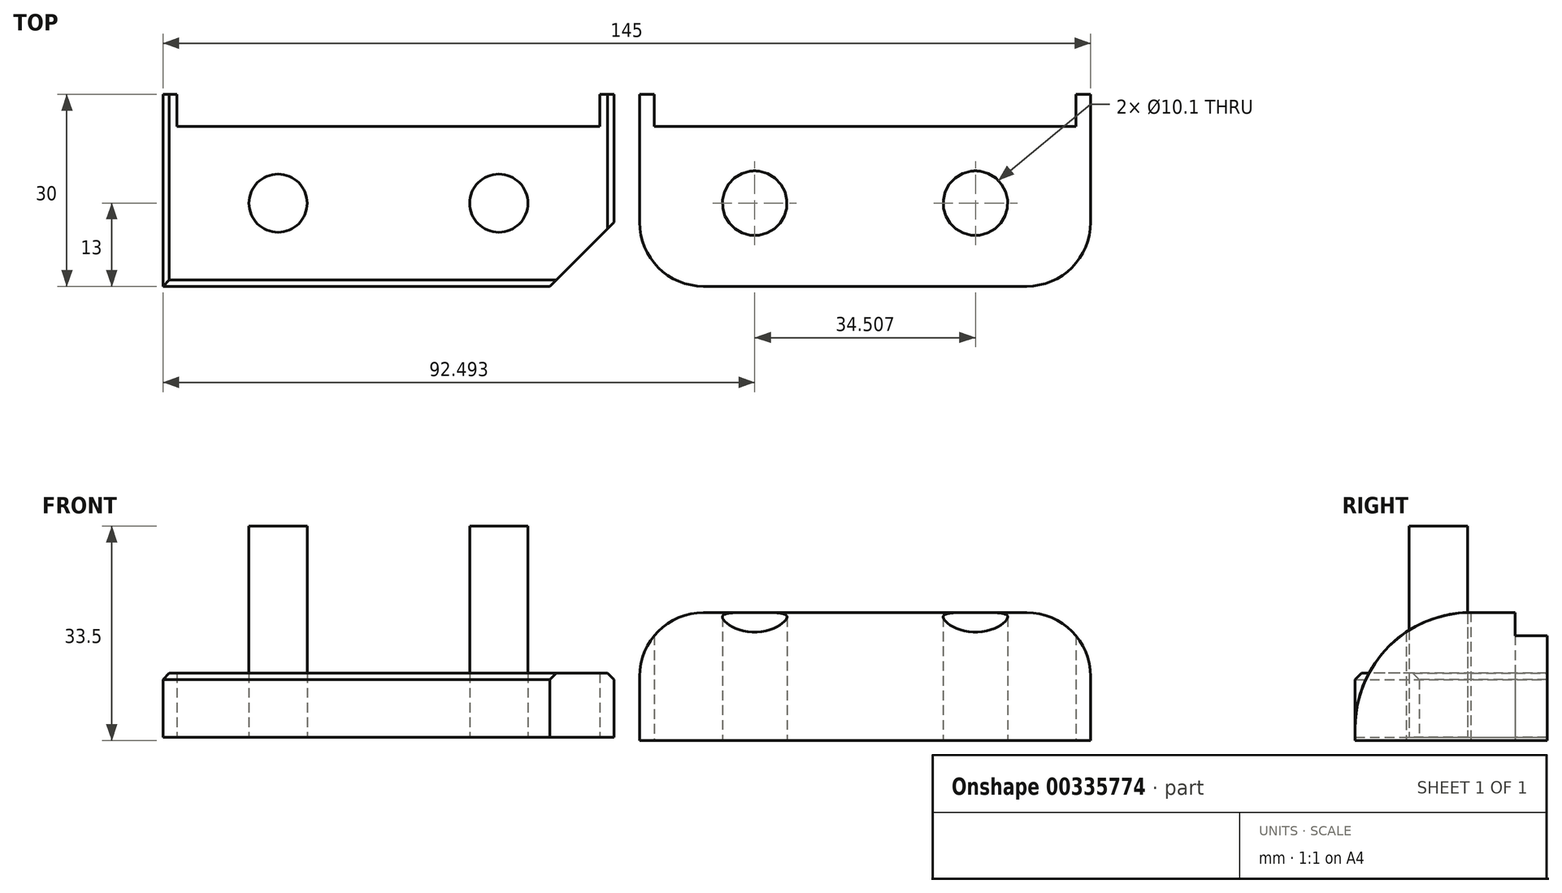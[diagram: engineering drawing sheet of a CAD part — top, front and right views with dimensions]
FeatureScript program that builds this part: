
annotation { "Feature Type Name" : "Feature", "Feature Type Description" : "" }
export const myFeature = defineFeature(function(context is Context, id is Id, definition is map)
    precondition{}
    {
        {
            var Q0;
            Q0=qCreatedBy(makeId("Front.planeOp"),FACE);
            var sketch = newSketch(context, id + "F0", { "sketchPlane" : qUnion([Q0])});
            skLineSegment(sketch, "E0.bottom", {"start": v(-53.86, 25) * mm, "end": v(16.64, 25) * mm});
            skLineSegment(sketch, "E0.top", {"start": v(-53.86, 5) * mm, "end": v(16.64, 5) * mm});
            skLineSegment(sketch, "E0.left", {"start": v(-53.86, 25) * mm, "end": v(-53.86, 5) * mm});
            skLineSegment(sketch, "E0.right", {"start": v(16.64, 25) * mm, "end": v(16.64, 5) * mm});
            skLineSegment(sketch, "E1.bottom", {"start": v(-53.86, 0) * mm, "end": v(16.64, 0) * mm});
            skLineSegment(sketch, "E1.top", {"start": v(-53.86, -10) * mm, "end": v(16.64, -10) * mm});
            skLineSegment(sketch, "E1.left", {"start": v(-53.86, 0) * mm, "end": v(-53.86, -10) * mm});
            skLineSegment(sketch, "E1.right", {"start": v(16.64, 0) * mm, "end": v(16.64, -10) * mm});
            skSolve(sketch);
        }
        {
            var Q0;
            Q0=makeQuery(id+"F0.imprint","IMPRINT",FACE,{"disambiguationData":[TD([[makeQuery(id+"F0.imprint","IMPRINT",EDGE,{"derivedFrom":sQuery(id+"F0.wireOp",EDGE,"E0.bottom")}),-1.0]])]});
            var Q1;
            Q1=makeQuery(id+"F0.imprint","IMPRINT",FACE,{"disambiguationData":[TD([[makeQuery(id+"F0.imprint","IMPRINT",EDGE,{"derivedFrom":sQuery(id+"F0.wireOp",EDGE,"E1.bottom")}),-1.0]])]});
            extrude(context, id + "F1", {"entities" : qUnion([Q0, Q1]), "depth" : 25 * mm});
        }
        {
            var Q0;
            Q0=qCreatedBy(makeId("Top.planeOp"),FACE);
            var sketch = newSketch(context, id + "F2", { "sketchPlane" : qUnion([Q0])});
            skPoint(sketch, "E2", {"position": v(-35.87, -12) * mm});
            skPoint(sketch, "E3", {"position": v(-1.36, -12) * mm});
            skSolve(sketch);
        }
        {
            var Q0;
            Q0=qCreatedBy(makeId("Top.planeOp"),FACE);
            var sketch = newSketch(context, id + "F3", { "sketchPlane" : qUnion([Q0])});
            skCircle(sketch, "E4", {"center": v(-35.87, -12) * mm, "radius": 4.55 * mm});
            skCircle(sketch, "E5", {"center": v(-1.36, -12) * mm, "radius": 4.55 * mm});
            skSolve(sketch);
        }
        {
            var Q0;
            Q0=makeQuery(id+"F3.imprint","IMPRINT",FACE,{"disambiguationData":[TD([[makeQuery(id+"F3.imprint","IMPRINT",EDGE,{"derivedFrom":sQuery(id+"F3.wireOp",EDGE,"E4")}),1.0]])]});
            var Q1;
            Q1=makeQuery(id+"F3.imprint","IMPRINT",FACE,{"disambiguationData":[TD([[makeQuery(id+"F3.imprint","IMPRINT",EDGE,{"derivedFrom":sQuery(id+"F3.wireOp",EDGE,"E5")}),1.0]])]});
            var Q2;
            Q2=sQuery(id+"F3.wireOp",EDGE,"E4");
            var Q3;
            Q3=sQuery(id+"F3.wireOp",EDGE,"E5");
            extrude(context, id + "F4", {"entities" : qUnion([Q0, Q1]), "surfaceEntities" : qUnion([Q2, Q3]), "depth" : 33 * mm});
        }
        {
            var Q0;
            Q0=makeQuery(id+"F1.opExtrude","CAP_FACE",FACE,{"disambiguationData":[OSD([sQuery(id+"F0.wireOp",EDGE,"E0.bottom"),sQuery(id+"F0.wireOp",EDGE,"E0.top"),sQuery(id+"F0.wireOp",EDGE,"E0.left"),sQuery(id+"F0.wireOp",EDGE,"E0.right")])],"isStart":true});
            var sketch = newSketch(context, id + "F5", { "sketchPlane" : qUnion([Q0])});
            skLineSegment(sketch, "E6.bottom", {"start": v(51.56, 25) * mm, "end": v(53.86, 25) * mm});
            skLineSegment(sketch, "E6.top", {"start": v(51.56, 5) * mm, "end": v(53.86, 5) * mm});
            skLineSegment(sketch, "E6.left", {"start": v(51.56, 25) * mm, "end": v(51.56, 5) * mm});
            skLineSegment(sketch, "E6.right", {"start": v(53.86, 25) * mm, "end": v(53.86, 5) * mm});
            skLineSegment(sketch, "E7.bottom", {"start": v(-16.64, 25) * mm, "end": v(-14.34, 25) * mm});
            skLineSegment(sketch, "E7.top", {"start": v(-16.64, 5) * mm, "end": v(-14.34, 5) * mm});
            skLineSegment(sketch, "E7.left", {"start": v(-16.64, 25) * mm, "end": v(-16.64, 5) * mm});
            skLineSegment(sketch, "E7.right", {"start": v(-14.34, 25) * mm, "end": v(-14.34, 5) * mm});
            skSolve(sketch);
        }
        {
            var Q0;
            Q0=makeQuery(id+"F5.imprint","IMPRINT",FACE,{"disambiguationData":[TD([[makeQuery(id+"F5.imprint","IMPRINT",EDGE,{"derivedFrom":sQuery(id+"F5.wireOp",EDGE,"E7.bottom")}),1.0]])]});
            var Q1;
            Q1=makeQuery(id+"F5.imprint","IMPRINT",FACE,{"disambiguationData":[TD([[makeQuery(id+"F5.imprint","IMPRINT",EDGE,{"derivedFrom":sQuery(id+"F5.wireOp",EDGE,"E6.bottom")}),1.0]])]});
            extrude(context, id + "F6", {"entities" : qUnion([Q0, Q1]), "operationType" : NewBodyOperationType.ADD, "depth" : 5 * mm});
        }
        {
            var Q0;
            Q0=qCreatedBy(makeId("Front.planeOp"),FACE);
            var sketch = newSketch(context, id + "F7", { "sketchPlane" : qUnion([Q0])});
            skLineSegment(sketch, "E8.bottom", {"start": v(-53.86, 0) * mm, "end": v(-51.66, 0) * mm});
            skLineSegment(sketch, "E8.top", {"start": v(-53.86, -10) * mm, "end": v(-51.66, -10) * mm});
            skLineSegment(sketch, "E8.left", {"start": v(-53.86, 0) * mm, "end": v(-53.86, -10) * mm});
            skLineSegment(sketch, "E8.right", {"start": v(-51.66, 0) * mm, "end": v(-51.66, -10) * mm});
            skLineSegment(sketch, "E9.bottom", {"start": v(16.64, 0) * mm, "end": v(14.44, 0) * mm});
            skLineSegment(sketch, "E9.top", {"start": v(16.64, -10) * mm, "end": v(14.44, -10) * mm});
            skLineSegment(sketch, "E9.left", {"start": v(16.64, 0) * mm, "end": v(16.64, -10) * mm});
            skLineSegment(sketch, "E9.right", {"start": v(14.44, 0) * mm, "end": v(14.44, -10) * mm});
            skSolve(sketch);
        }
        {
            var Q0;
            Q0=makeQuery(id+"F7.imprint","IMPRINT",FACE,{"disambiguationData":[TD([[makeQuery(id+"F7.imprint","IMPRINT",EDGE,{"derivedFrom":sQuery(id+"F7.wireOp",EDGE,"E9.bottom")}),1.0]])]});
            var Q1;
            Q1=makeQuery(id+"F7.imprint","IMPRINT",FACE,{"disambiguationData":[TD([[makeQuery(id+"F7.imprint","IMPRINT",EDGE,{"derivedFrom":sQuery(id+"F7.wireOp",EDGE,"E8.bottom")}),-1.0]])]});
            extrude(context, id + "F8", {"entities" : qUnion([Q0, Q1]), "operationType" : NewBodyOperationType.ADD, "oppositeDirection" : true, "depth" : 5 * mm});
        }
        {
            var Q0;
            Q0=sQuery(id+"F2.wireOp",VERTEX,"E2");
            var Q1;
            Q1=sQuery(id+"F2.wireOp",VERTEX,"E3");
            var Q2;
            Q2=makeQuery(id+"F1.opExtrude","SWEPT_BODY",BODY,{"disambiguationData":[OSD([sQuery(id+"F0.wireOp",EDGE,"E0.bottom"),sQuery(id+"F0.wireOp",EDGE,"E0.top"),sQuery(id+"F0.wireOp",EDGE,"E0.left"),sQuery(id+"F0.wireOp",EDGE,"E0.right")])]});
            hole(context, id + "F9", {"style" : HoleStyle.SIMPLE, "endStyle" : HoleEndStyle.THROUGH, "oppositeDirection" : true, "holeDiameter" : 10.1 * mm, "tappedDepth" : 12 * mm, "tapClearance" : 3, "startFromSketch" : true, "locations" : qUnion([Q0, Q1]), "scope" : qUnion([Q2])});
        }
        {
            var Q0;
            Q0=makeQuery(id+"F1.opExtrude","SWEPT_BODY",BODY,{"disambiguationData":[OSD([sQuery(id+"F0.wireOp",EDGE,"E0.bottom"),sQuery(id+"F0.wireOp",EDGE,"E0.top"),sQuery(id+"F0.wireOp",EDGE,"E0.left"),sQuery(id+"F0.wireOp",EDGE,"E0.right")])]});
            transform(context, id + "F10", {"entities" : qUnion([Q0]), "transformType" : TransformType.TRANSLATION_3D, "dx" : -14.5 * mm, "dy" : 0 * mm, "dz" : 2.8 * mm, "makeCopy" : false});
        }
        {
            var Q0;
            Q0=makeQuery(id+"F1.opExtrude","SWEPT_BODY",BODY,{"disambiguationData":[OSD([sQuery(id+"F0.wireOp",EDGE,"E0.bottom"),sQuery(id+"F0.wireOp",EDGE,"E0.top"),sQuery(id+"F0.wireOp",EDGE,"E0.left"),sQuery(id+"F0.wireOp",EDGE,"E0.right")])]});
            transform(context, id + "F11", {"entities" : qUnion([Q0]), "transformType" : TransformType.TRANSLATION_3D, "dx" : 66.3 * mm, "dy" : 0 * mm, "dz" : -8.2 * mm, "makeCopy" : false});
        }
        {
            var Q0;
            Q0=makeQuery(id+"F1.opExtrude","SWEPT_BODY",BODY,{"disambiguationData":[OSD([sQuery(id+"F0.wireOp",EDGE,"E1.bottom"),sQuery(id+"F0.wireOp",EDGE,"E1.top"),sQuery(id+"F0.wireOp",EDGE,"E1.left"),sQuery(id+"F0.wireOp",EDGE,"E1.right")])]});
            var Q1;
            Q1=makeQuery(id+"F4.opExtrude","SWEPT_BODY",BODY,{"disambiguationData":[OSD([sQuery(id+"F3.wireOp",EDGE,"E4")])]});
            var Q2;
            Q2=makeQuery(id+"F4.opExtrude","SWEPT_BODY",BODY,{"disambiguationData":[OSD([sQuery(id+"F3.wireOp",EDGE,"E5")])]});
            transform(context, id + "F12", {"entities" : qUnion([Q0, Q1, Q2]), "transformType" : TransformType.TRANSLATION_3D, "dx" : -25.1 * mm, "dy" : 0 * mm, "dz" : 26.8 * mm, "makeCopy" : false});
        }
        {
            var Q0;
            Q0=makeQuery(id+"F1.opExtrude","CAP_EDGE",EDGE,{"disambiguationData":[OSD([sQuery(id+"F0.wireOp",EDGE,"E0.bottom")])],"isStart":false});
            fillet(context, id + "F13", {"entities" : qUnion([Q0]), "radius" : 18 * mm, "tangentPropagation" : true, "allowEdgeOverflow" : false});
        }
        {
            var Q0;
            Q0=makeQuery(id+"F1.opExtrude","SWEPT_BODY",BODY,{"disambiguationData":[OSD([sQuery(id+"F0.wireOp",EDGE,"E1.bottom"),sQuery(id+"F0.wireOp",EDGE,"E1.top"),sQuery(id+"F0.wireOp",EDGE,"E1.left"),sQuery(id+"F0.wireOp",EDGE,"E1.right")])]});
            var Q1;
            Q1=makeQuery(id+"F4.opExtrude","SWEPT_BODY",BODY,{"disambiguationData":[OSD([sQuery(id+"F3.wireOp",EDGE,"E4")])]});
            var Q2;
            Q2=makeQuery(id+"F4.opExtrude","SWEPT_BODY",BODY,{"disambiguationData":[OSD([sQuery(id+"F3.wireOp",EDGE,"E5")])]});
            transform(context, id + "F14", {"entities" : qUnion([Q0, Q1, Q2]), "transformType" : TransformType.TRANSLATION_3D, "dx" : 4.4 * mm, "dy" : 0 * mm, "dz" : -6.8 * mm, "makeCopy" : false});
        }
        {
            var Q0;
            Q0=makeQuery(id+"F1.opExtrude","CAP_EDGE",EDGE,{"disambiguationData":[OSD([sQuery(id+"F0.wireOp",EDGE,"E1.bottom")])],"isStart":false});
            chamfer(context, id + "F15", {"entities" : qUnion([Q0]), "width" : 1 * mm, "tangentPropagation" : true});
        }
        {
            var Q0;
            Q0=makeQuery(id+"F8.boolean.opBoolean","MERGE",EDGE,{"derivedFrom":[makeQuery(id+"F1.opExtrude","SWEPT_EDGE",EDGE,{"disambiguationData":[OSD([sQuery(id+"F0.wireOp",EDGE,"E1.bottom"),sQuery(id+"F0.wireOp",EDGE,"E1.right")])]}),makeQuery(id+"F8.opExtrude","SWEPT_EDGE",EDGE,{"disambiguationData":[OSD([sQuery(id+"F7.wireOp",EDGE,"E9.bottom"),sQuery(id+"F7.wireOp",EDGE,"E9.left")])]})]});
            var Q1;
            Q1=makeQuery(id+"F8.boolean.opBoolean","MERGE",EDGE,{"derivedFrom":[makeQuery(id+"F1.opExtrude","SWEPT_EDGE",EDGE,{"disambiguationData":[OSD([sQuery(id+"F0.wireOp",EDGE,"E1.bottom"),sQuery(id+"F0.wireOp",EDGE,"E1.left")])]}),makeQuery(id+"F8.opExtrude","SWEPT_EDGE",EDGE,{"disambiguationData":[OSD([sQuery(id+"F7.wireOp",EDGE,"E8.bottom"),sQuery(id+"F7.wireOp",EDGE,"E8.left")])]})]});
            chamfer(context, id + "F16", {"entities" : qUnion([Q0, Q1]), "width" : 1 * mm, "tangentPropagation" : true});
        }
        {
            var Q0;
            Q0=makeQuery(id+"F13.opFillet","BLEND_EDGE",EDGE,{"blendedFrom":[makeQuery(id+"F1.opExtrude","CAP_EDGE",EDGE,{"disambiguationData":[OSD([sQuery(id+"F0.wireOp",EDGE,"E0.bottom")])],"isStart":false}),makeQuery(id+"F6.boolean.opBoolean","MERGE",FACE,{"derivedFrom":[makeQuery(id+"F1.opExtrude","SWEPT_FACE",FACE,{"disambiguationData":[OSD([sQuery(id+"F0.wireOp",EDGE,"E0.right")])]}),makeQuery(id+"F6.opExtrude","SWEPT_FACE",FACE,{"disambiguationData":[OSD([sQuery(id+"F5.wireOp",EDGE,"E7.left")])]})]})],"blendedInto":[makeQuery(id+"F6.boolean.opBoolean","MERGE",FACE,{"derivedFrom":[makeQuery(id+"F1.opExtrude","SWEPT_FACE",FACE,{"disambiguationData":[OSD([sQuery(id+"F0.wireOp",EDGE,"E0.right")])]}),makeQuery(id+"F6.opExtrude","SWEPT_FACE",FACE,{"disambiguationData":[OSD([sQuery(id+"F5.wireOp",EDGE,"E7.left")])]})]})]});
            fillet(context, id + "F17", {"entities" : qUnion([Q0]), "radius" : 10 * mm, "tangentPropagation" : true, "allowEdgeOverflow" : false});
        }
        {
            var Q0;
            Q0=makeQuery(id+"F13.opFillet","BLEND_EDGE",EDGE,{"blendedFrom":[makeQuery(id+"F1.opExtrude","CAP_EDGE",EDGE,{"disambiguationData":[OSD([sQuery(id+"F0.wireOp",EDGE,"E0.bottom")])],"isStart":false}),makeQuery(id+"F6.boolean.opBoolean","MERGE",FACE,{"derivedFrom":[makeQuery(id+"F1.opExtrude","SWEPT_FACE",FACE,{"disambiguationData":[OSD([sQuery(id+"F0.wireOp",EDGE,"E0.left")])]}),makeQuery(id+"F6.opExtrude","SWEPT_FACE",FACE,{"disambiguationData":[OSD([sQuery(id+"F5.wireOp",EDGE,"E6.right")])]})]})],"blendedInto":[makeQuery(id+"F6.boolean.opBoolean","MERGE",FACE,{"derivedFrom":[makeQuery(id+"F1.opExtrude","SWEPT_FACE",FACE,{"disambiguationData":[OSD([sQuery(id+"F0.wireOp",EDGE,"E0.left")])]}),makeQuery(id+"F6.opExtrude","SWEPT_FACE",FACE,{"disambiguationData":[OSD([sQuery(id+"F5.wireOp",EDGE,"E6.right")])]})]})]});
            fillet(context, id + "F18", {"entities" : qUnion([Q0]), "radius" : 10 * mm, "tangentPropagation" : true, "allowEdgeOverflow" : false});
        }
        {
            var Q0;
            Q0=makeQuery(id+"F4.opExtrude","SWEPT_BODY",BODY,{"disambiguationData":[OSD([sQuery(id+"F3.wireOp",EDGE,"E4")])]});
            var Q1;
            Q1=makeQuery(id+"F4.opExtrude","SWEPT_BODY",BODY,{"disambiguationData":[OSD([sQuery(id+"F3.wireOp",EDGE,"E5")])]});
            var Q2;
            Q2=qCreatedBy(makeId("Top.planeOp"),FACE);
            transform(context, id + "F19", {"entities" : qUnion([Q0, Q1]), "transformType" : TransformType.TRANSLATION_DISTANCE, "transformDirection" : qUnion([Q2]), "distance" : 10 * mm, "oppositeDirection" : true, "makeCopy" : false});
        }
        {
            var Q0;
            Q0=makeQuery(id+"F1.opExtrude","SWEPT_BODY",BODY,{"disambiguationData":[OSD([sQuery(id+"F0.wireOp",EDGE,"E1.bottom"),sQuery(id+"F0.wireOp",EDGE,"E1.top"),sQuery(id+"F0.wireOp",EDGE,"E1.left"),sQuery(id+"F0.wireOp",EDGE,"E1.right")])]});
            var Q1;
            Q1=makeQuery(id+"F4.opExtrude","SWEPT_BODY",BODY,{"disambiguationData":[OSD([sQuery(id+"F3.wireOp",EDGE,"E4")])]});
            var Q2;
            Q2=makeQuery(id+"F4.opExtrude","SWEPT_BODY",BODY,{"disambiguationData":[OSD([sQuery(id+"F3.wireOp",EDGE,"E5")])]});
            transform(context, id + "F20", {"entities" : qUnion([Q0, Q1, Q2]), "transformType" : TransformType.TRANSLATION_3D, "dx" : -2 * mm, "dy" : 0 * mm, "dz" : -9.9 * mm, "makeCopy" : false});
        }
        {
            var Q0;
            Q0=makeQuery(id+"F1.opExtrude","CAP_EDGE",EDGE,{"disambiguationData":[OSD([sQuery(id+"F0.wireOp",EDGE,"E1.right")])],"isStart":false});
            chamfer(context, id + "F21", {"entities" : qUnion([Q0]), "width" : 10 * mm, "tangentPropagation" : true});
        }
    });
